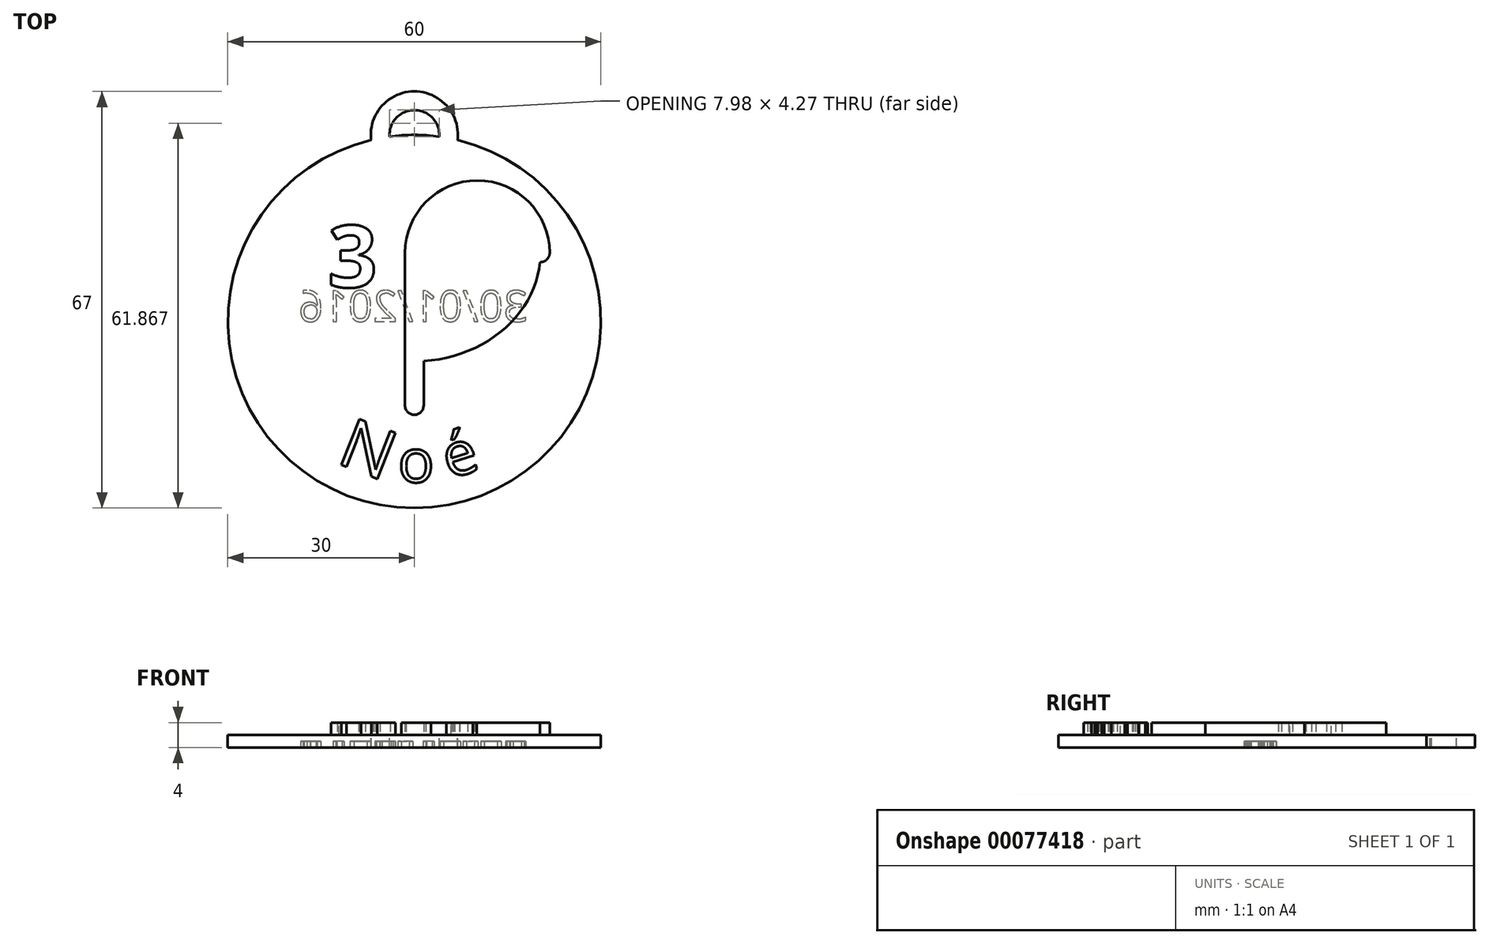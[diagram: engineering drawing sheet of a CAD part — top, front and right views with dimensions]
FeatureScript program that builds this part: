
annotation { "Feature Type Name" : "Feature", "Feature Type Description" : "" }
export const myFeature = defineFeature(function(context is Context, id is Id, definition is map)
    precondition{}
    {
        {
            var Q0;
            Q0=qCreatedBy(makeId("Top.planeOp"),FACE);
            var sketch = newSketch(context, id + "F0", { "sketchPlane" : qUnion([Q0])});
            skCircle(sketch, "E0", {"center": v(0, 0) * mm, "radius": 30 * mm});
            skSolve(sketch);
        }
        {
            var Q0;
            Q0=qSketchRegion(id+"F0",true);
            extrude(context, id + "F1", {"entities" : qUnion([Q0]), "oppositeDirection" : true, "depth" : 2 * mm});
        }
        {
            var Q0;
            Q0=qCreatedBy(makeId("Top.planeOp"),FACE);
            var sketch = newSketch(context, id + "F2", { "sketchPlane" : qUnion([Q0])});
            skEllipticalArc(sketch, "E1", {});
            skLineSegment(sketch, "E2", {"start": v(0, 0) * mm, "end": v(0, 30) * mm, "construction": true});
            skLineSegment(sketch, "E3", {"start": v(0, 11.04) * mm, "end": v(0, -13.5) * mm});
            skArc(sketch, "E4", {"start": v(20.27, 11.04) * mm, "mid": v(10.13, 21.17) * mm, "end": v(0, 11.04) * mm});
            skLineSegment(sketch, "E5", {"start": v(0, 11.04) * mm, "end": v(-16.84, 20.76) * mm, "construction": true});
            skLineSegment(sketch, "E6", {"start": v(0, 11.04) * mm, "end": v(-20.27, 11.04) * mm, "construction": true});
            skArc(sketch, "E7.0.startCap", {"start": v(-1.5, 11.04) * mm, "mid": v(0, 12.54) * mm, "end": v(1.5, 11.04) * mm});
            skArc(sketch, "E7.0.endCap", {"start": v(1.5, -13.5) * mm, "mid": v(0, -15) * mm, "end": v(-1.5, -13.5) * mm});
            skLineSegment(sketch, "E7.0.left", {"start": v(1.5, 11.04) * mm, "end": v(1.5, -13.5) * mm});
            skLineSegment(sketch, "E7.0.right", {"start": v(-1.5, 11.04) * mm, "end": v(-1.5, -13.5) * mm});
            skArc(sketch, "E8.0.startCap", {"start": v(21.77, 11.04) * mm, "mid": v(20.27, 9.54) * mm, "end": v(18.77, 11.04) * mm});
            skArc(sketch, "E8.0.endCap", {"start": v(1.5, 11.04) * mm, "mid": v(0, 9.54) * mm, "end": v(-1.5, 11.04) * mm});
            skArc(sketch, "E8.0.left", {"start": v(18.77, 11.04) * mm, "mid": v(10.13, 19.67) * mm, "end": v(1.5, 11.04) * mm});
            skArc(sketch, "E8.0.right", {"start": v(21.77, 11.04) * mm, "mid": v(10.13, 22.67) * mm, "end": v(-1.5, 11.04) * mm});
            skArc(sketch, "E8.1.startCap", {"start": v(-18.02, 21.68) * mm, "mid": v(-15.91, 21.95) * mm, "end": v(-15.65, 19.84) * mm});
            skArc(sketch, "E8.1.endCap", {"start": v(18.77, 11.04) * mm, "mid": v(20.27, 12.54) * mm, "end": v(21.77, 11.04) * mm});
            skFitSpline(sketch, "E8.1.left", {"points": [v(18.7, 9.5) * mm, v(18.8, 11.04) * mm, v(18.7, 12.6) * mm, v(18.36, 14.63) * mm, v(17.66, 16.6) * mm, v(16.63, 18.49) * mm, v(15.37, 20.3) * mm, v(13.44, 22.32) * mm, v(11.07, 24) * mm, v(8.94, 25.1) * mm, v(6.7, 26.01) * mm, v(4.32, 26.63) * mm, v(1.87, 26.95) * mm, v(0, 27.03) * mm, v(-1.87, 26.95) * mm, v(-4.32, 26.63) * mm, v(-6.7, 26.01) * mm, v(-8.94, 25.1) * mm, v(-11.07, 24) * mm, v(-13.44, 22.32) * mm, v(-15.37, 20.3) * mm, v(-16.63, 18.49) * mm, v(-17.66, 16.6) * mm, v(-18.36, 14.63) * mm, v(-18.7, 12.6) * mm, v(-18.8, 11.04) * mm, v(-18.7, 9.5) * mm, v(-18.36, 7.46) * mm, v(-17.66, 5.48) * mm, v(-16.63, 3.6) * mm, v(-15.37, 1.8) * mm, v(-13.44, -0.24) * mm, v(-11.07, -1.92) * mm, v(-8.94, -3.02) * mm, v(-6.7, -3.93) * mm, v(-4.32, -4.55) * mm, v(-1.87, -4.86) * mm, v(0, -4.94) * mm, v(1.87, -4.86) * mm, v(4.32, -4.55) * mm, v(6.7, -3.93) * mm, v(8.94, -3.02) * mm, v(11.07, -1.92) * mm, v(13.44, -0.24) * mm, v(15.37, 1.8) * mm, v(16.63, 3.6) * mm, v(17.66, 5.48) * mm, v(18.36, 7.46) * mm, v(18.7, 9.5) * mm, v(18.8, 11.04) * mm, v(18.7, 12.6) * mm]});
            skFitSpline(sketch, "E8.1.right", {"points": [v(21.7, 9.15) * mm, v(21.8, 11.04) * mm, v(21.7, 12.93) * mm, v(21.27, 15.42) * mm, v(20.42, 17.81) * mm, v(19.18, 20.07) * mm, v(17.69, 22.22) * mm, v(15.4, 24.61) * mm, v(12.65, 26.56) * mm, v(10.2, 27.83) * mm, v(7.62, 28.88) * mm, v(4.92, 29.58) * mm, v(2.12, 29.94) * mm, v(0, 30.03) * mm, v(-2.12, 29.94) * mm, v(-4.92, 29.58) * mm, v(-7.62, 28.88) * mm, v(-10.2, 27.83) * mm, v(-12.65, 26.56) * mm, v(-15.4, 24.61) * mm, v(-17.69, 22.22) * mm, v(-19.18, 20.07) * mm, v(-20.42, 17.81) * mm, v(-21.27, 15.42) * mm, v(-21.7, 12.93) * mm, v(-21.8, 11.04) * mm, v(-21.7, 9.15) * mm, v(-21.27, 6.67) * mm, v(-20.42, 4.27) * mm, v(-19.18, 2) * mm, v(-17.69, -0.14) * mm, v(-15.4, -2.53) * mm, v(-12.65, -4.48) * mm, v(-10.2, -5.75) * mm, v(-7.62, -6.8) * mm, v(-4.92, -7.5) * mm, v(-2.12, -7.86) * mm, v(0, -7.95) * mm, v(2.12, -7.86) * mm, v(4.92, -7.5) * mm, v(7.62, -6.8) * mm, v(10.2, -5.75) * mm, v(12.65, -4.48) * mm, v(15.4, -2.53) * mm, v(17.69, -0.14) * mm, v(19.18, 2) * mm, v(20.42, 4.27) * mm, v(21.27, 6.67) * mm, v(21.7, 9.15) * mm, v(21.8, 11.04) * mm, v(21.7, 12.93) * mm]});
            const initialGuessF2  = {"E1": [0, 0.011041626236194823, 1, 0, 0.020266667008310185, 0.017458373763805178, 2.5511335140588507, 0]};
            skSetInitialGuess(sketch, initialGuessF2);
            skSolve(sketch);
        }
        {
            var Q0;
            {var subQ0=sQuery(id+"F2.wireOp",EDGE,"E8.1.startCap");Q0=makeQuery(id+"F2.imprint","IMPRINT",FACE,{"disambiguationData":[TD([[makeQuery(id+"F2.imprint","IMPRINT",EDGE,{"derivedFrom":subQ0}),-1.0]])]});}
            var Q1;
            {var subQ0=sQuery(id+"F2.wireOp",EDGE,"E7.0.right");var subQ1=sQuery(id+"F2.wireOp",EDGE,"E1");var subQ2=makeQuery(id+"F2.imprint","INTERSECT",VERTEX,{"derivedFrom":[subQ1,subQ0]});Q1=makeQuery(id+"F2.imprint","IMPRINT",FACE,{"disambiguationData":[TD([[makeQuery(id+"F2.imprint","IMPRINT",EDGE,{"disambiguationData":[TD([[subQ2,-1.0]])],"derivedFrom":subQ1}),1.0]])]});}
            var Q2;
            {var subQ0=sQuery(id+"F2.wireOp",EDGE,"E3");var subQ1=sQuery(id+"F2.wireOp",EDGE,"E1");var subQ2=makeQuery(id+"F2.imprint","INTERSECT",VERTEX,{"derivedFrom":[subQ1,subQ0]});Q2=makeQuery(id+"F2.imprint","IMPRINT",FACE,{"disambiguationData":[TD([[makeQuery(id+"F2.imprint","IMPRINT",EDGE,{"disambiguationData":[TD([[subQ2,-1.0]])],"derivedFrom":subQ1}),1.0]])]});}
            var Q3;
            {var subQ0=sQuery(id+"F2.wireOp",EDGE,"E7.0.right");var subQ1=sQuery(id+"F2.wireOp",EDGE,"E1");var subQ2=makeQuery(id+"F2.imprint","INTERSECT",VERTEX,{"derivedFrom":[subQ1,subQ0]});Q3=makeQuery(id+"F2.imprint","IMPRINT",FACE,{"disambiguationData":[TD([[makeQuery(id+"F2.imprint","IMPRINT",EDGE,{"disambiguationData":[TD([[subQ2,-1.0]])],"derivedFrom":subQ1}),-1.0]])]});}
            var Q4;
            {var subQ0=sQuery(id+"F2.wireOp",EDGE,"E3");var subQ1=sQuery(id+"F2.wireOp",EDGE,"E1");var subQ2=makeQuery(id+"F2.imprint","INTERSECT",VERTEX,{"derivedFrom":[subQ1,subQ0]});Q4=makeQuery(id+"F2.imprint","IMPRINT",FACE,{"disambiguationData":[TD([[makeQuery(id+"F2.imprint","IMPRINT",EDGE,{"disambiguationData":[TD([[subQ2,-1.0]])],"derivedFrom":subQ1}),-1.0]])]});}
            var Q5;
            {var subQ0=sQuery(id+"F2.wireOp",EDGE,"E7.0.left");var subQ1=sQuery(id+"F2.wireOp",EDGE,"E1");var subQ2=makeQuery(id+"F2.imprint","INTERSECT",VERTEX,{"derivedFrom":[subQ1,subQ0]});Q5=makeQuery(id+"F2.imprint","IMPRINT",FACE,{"disambiguationData":[TD([[makeQuery(id+"F2.imprint","IMPRINT",EDGE,{"disambiguationData":[TD([[subQ2,-1.0]])],"derivedFrom":subQ1}),-1.0]])]});}
            var Q6;
            {var subQ0=sQuery(id+"F2.wireOp",EDGE,"E7.0.left");var subQ1=sQuery(id+"F2.wireOp",EDGE,"E1");var subQ2=makeQuery(id+"F2.imprint","INTERSECT",VERTEX,{"derivedFrom":[subQ1,subQ0]});Q6=makeQuery(id+"F2.imprint","IMPRINT",FACE,{"disambiguationData":[TD([[makeQuery(id+"F2.imprint","IMPRINT",EDGE,{"disambiguationData":[TD([[subQ2,-1.0]])],"derivedFrom":subQ1}),1.0]])]});}
            var Q7;
            {var subQ0=sQuery(id+"F2.wireOp",EDGE,"E4");var subQ1=sQuery(id+"F2.wireOp",EDGE,"E1");var subQ2=makeQuery(id+"F2.imprint","INTERSECT",VERTEX,{"derivedFrom":[subQ1,subQ0]});Q7=makeQuery(id+"F2.imprint","IMPRINT",FACE,{"disambiguationData":[TD([[makeQuery(id+"F2.imprint","IMPRINT",EDGE,{"disambiguationData":[TD([[subQ2,1.0]])],"derivedFrom":subQ1}),-1.0]])]});}
            var Q8;
            {var subQ0=sQuery(id+"F2.wireOp",EDGE,"E4");var subQ1=sQuery(id+"F2.wireOp",EDGE,"E1");var subQ2=makeQuery(id+"F2.imprint","INTERSECT",VERTEX,{"derivedFrom":[subQ1,subQ0]});Q8=makeQuery(id+"F2.imprint","IMPRINT",FACE,{"disambiguationData":[TD([[makeQuery(id+"F2.imprint","IMPRINT",EDGE,{"disambiguationData":[TD([[subQ2,1.0]])],"derivedFrom":subQ1}),1.0]])]});}
            var Q9;
            {var subQ5=sQuery(id+"F2.wireOp",EDGE,"E8.0.left");Q9=makeQuery(id+"F2.imprint","IMPRINT",FACE,{"disambiguationData":[TD([[makeQuery(id+"F2.imprint","IMPRINT",EDGE,{"derivedFrom":subQ5}),-1.0]])]});}
            var Q10;
            {var subQ5=sQuery(id+"F2.wireOp",EDGE,"E8.0.right");Q10=makeQuery(id+"F2.imprint","IMPRINT",FACE,{"disambiguationData":[TD([[makeQuery(id+"F2.imprint","IMPRINT",EDGE,{"derivedFrom":subQ5}),1.0]])]});}
            var Q11;
            {var subQ0=sQuery(id+"F2.wireOp",EDGE,"E4");var subQ1=sQuery(id+"F2.wireOp",EDGE,"E3");var subQ2=makeQuery(id+"F2.imprint","INTERSECT",VERTEX,{"derivedFrom":[subQ1,subQ0]});Q11=makeQuery(id+"F2.imprint","IMPRINT",FACE,{"disambiguationData":[TD([[makeQuery(id+"F2.imprint","IMPRINT",EDGE,{"disambiguationData":[TD([[subQ2,-1.0]])],"derivedFrom":subQ1}),-1.0]])]});}
            var Q12;
            {var subQ0=sQuery(id+"F2.wireOp",EDGE,"E4");var subQ1=sQuery(id+"F2.wireOp",EDGE,"E3");var subQ2=makeQuery(id+"F2.imprint","INTERSECT",VERTEX,{"derivedFrom":[subQ1,subQ0]});Q12=makeQuery(id+"F2.imprint","IMPRINT",FACE,{"disambiguationData":[TD([[makeQuery(id+"F2.imprint","IMPRINT",EDGE,{"disambiguationData":[TD([[subQ2,-1.0]])],"derivedFrom":subQ1}),1.0]])]});}
            var Q13;
            {var subQ0=sQuery(id+"F2.wireOp",EDGE,"E8.0.endCap");var subQ1=sQuery(id+"F2.wireOp",EDGE,"E3");var subQ2=makeQuery(id+"F2.imprint","INTERSECT",VERTEX,{"derivedFrom":[subQ1,subQ0]});Q13=makeQuery(id+"F2.imprint","IMPRINT",FACE,{"disambiguationData":[TD([[makeQuery(id+"F2.imprint","IMPRINT",EDGE,{"disambiguationData":[TD([[subQ2,-1.0]])],"derivedFrom":subQ1}),-1.0]])]});}
            var Q14;
            {var subQ0=sQuery(id+"F2.wireOp",EDGE,"E8.0.endCap");var subQ1=sQuery(id+"F2.wireOp",EDGE,"E3");var subQ2=makeQuery(id+"F2.imprint","INTERSECT",VERTEX,{"derivedFrom":[subQ1,subQ0]});Q14=makeQuery(id+"F2.imprint","IMPRINT",FACE,{"disambiguationData":[TD([[makeQuery(id+"F2.imprint","IMPRINT",EDGE,{"disambiguationData":[TD([[subQ2,-1.0]])],"derivedFrom":subQ1}),1.0]])]});}
            var Q15;
            {var subQ1=sQuery(id+"F2.wireOp",EDGE,"E7.0.endCap");Q15=makeQuery(id+"F2.imprint","IMPRINT",FACE,{"disambiguationData":[TD([[makeQuery(id+"F2.imprint","IMPRINT",EDGE,{"derivedFrom":subQ1}),-1.0]])]});}
            extrude(context, id + "F3", {"entities" : qUnion([Q0, Q1, Q2, Q3, Q4, Q5, Q6, Q7, Q8, Q9, Q10, Q11, Q12, Q13, Q14, Q15]), "operationType" : NewBodyOperationType.ADD, "depth" : 2 * mm});
        }
        {
            var Q0;
            Q0=qCreatedBy(makeId("Top.planeOp"),FACE);
            var sketch = newSketch(context, id + "F4", { "sketchPlane" : qUnion([Q0])});
            skText(sketch, "E9", { "text": "3", "fontName": "OpenSans-Bold.ttf"});
            skText(sketch, "E10", { "text": "D", "fontName": "OpenSans-Bold.ttf"});
            const initialGuessF4  = {"E9": [-0.0139, 0.0055, 1, 0, 0.01], "E10": [0.0055, 0.0055, 1, 0, 0.01]};
            skSetInitialGuess(sketch, initialGuessF4);
            skSolve(sketch);
        }
        {
            var Q0;
            Q0=qSketchRegion(id+"F4",true);
            extrude(context, id + "F5", {"entities" : qUnion([Q0]), "operationType" : NewBodyOperationType.ADD, "depth" : 2 * mm});
        }
        {
            var Q0;
            {var subQ8=sQuery(id+"F0.wireOp",EDGE,"E0");Q0=makeQuery(id+"F3.boolean.opBoolean","SPLIT",FACE,{"disambiguationData":[TD([makeQuery(id+"F1.opExtrude","SWEPT_FACE",FACE,{"disambiguationData":[OSD([subQ8])]})])],"derivedFrom":makeQuery(id+"F1.opExtrude","CAP_FACE",FACE,{"disambiguationData":[OSD([subQ8])],"isStart":true})});}
            var sketch = newSketch(context, id + "F6", { "sketchPlane" : qUnion([Q0])});
            skCircle(sketch, "E11.0", {"center": v(0, 0) * mm, "radius": 26 * mm, "construction": true});
            skText(sketch, "E12", { "text": "N", "fontName": "OpenSans-Regular.ttf"});
            skText(sketch, "E13", { "text": "o", "fontName": "OpenSans-Regular.ttf"});
            skText(sketch, "E14", { "text": "é", "fontName": "OpenSans-Regular.ttf"});
            const initialGuessF6  = {"E12": [-0.01273, -0.02267, 0.93191, -0.36269, 0.008], "E13": [-0.00266, -0.02586, 1, 0, 0.007], "E14": [0.00565, -0.02538, 0.95098, 0.30925, 0.007]};
            skSetInitialGuess(sketch, initialGuessF6);
            skSolve(sketch);
        }
        {
            var Q0;
            Q0=qSketchRegion(id+"F6",true);
            extrude(context, id + "F7", {"entities" : qUnion([Q0]), "operationType" : NewBodyOperationType.ADD, "depth" : 2 * mm});
        }
        {
            var Q0;
            Q0=qCreatedBy(makeId("Top.planeOp"),FACE);
            var sketch = newSketch(context, id + "F8", { "sketchPlane" : qUnion([Q0])});
            skArc(sketch, "E15", {"start": v(5.48, 29.5) * mm, "mid": v(0, 35.5) * mm, "end": v(-5.48, 29.5) * mm});
            skArc(sketch, "E16.0.startCap", {"start": v(6.97, 29.36) * mm, "mid": v(5.34, 28) * mm, "end": v(3.98, 29.63) * mm});
            skArc(sketch, "E16.0.endCap", {"start": v(-3.98, 29.63) * mm, "mid": v(-5.34, 28) * mm, "end": v(-6.97, 29.36) * mm});
            skArc(sketch, "E16.0.left", {"start": v(3.98, 29.63) * mm, "mid": v(0, 34) * mm, "end": v(-3.98, 29.63) * mm});
            skArc(sketch, "E16.0.right", {"start": v(6.97, 29.36) * mm, "mid": v(0, 37) * mm, "end": v(-6.97, 29.36) * mm});
            skSolve(sketch);
        }
        {
            var Q0;
            Q0=qSketchRegion(id+"F8",true);
            extrude(context, id + "F9", {"entities" : qUnion([Q0]), "operationType" : NewBodyOperationType.ADD, "oppositeDirection" : true, "depth" : 2 * mm});
        }
        {
            var Q0;
            Q0=makeQuery(id+"F9.boolean.opBoolean","MERGE",FACE,{"derivedFrom":[makeQuery(id+"F1.opExtrude","CAP_FACE",FACE,{"disambiguationData":[OSD([sQuery(id+"F0.wireOp",EDGE,"E0")])],"isStart":false}),makeQuery(id+"F9.opExtrude","CAP_FACE",FACE,{"disambiguationData":[OSD([sQuery(id+"F8.wireOp",EDGE,"E16.0.startCap"),sQuery(id+"F8.wireOp",EDGE,"E16.0.endCap"),sQuery(id+"F8.wireOp",EDGE,"E16.0.left"),sQuery(id+"F8.wireOp",EDGE,"E16.0.right")])],"isStart":false})]});
            var sketch = newSketch(context, id + "F10", { "sketchPlane" : qUnion([Q0])});
            skText(sketch, "E17", { "text": "30/01/2016", "fontName": "OpenSans-Regular.ttf"});
            const initialGuessF10  = {"E17": [0.01826, 0, -1, 0, 0.005]};
            skSetInitialGuess(sketch, initialGuessF10);
            skSolve(sketch);
        }
        {
            var Q0;
            Q0=qSketchRegion(id+"F10",true);
            extrude(context, id + "F11", {"entities" : qUnion([Q0]), "operationType" : NewBodyOperationType.REMOVE, "oppositeDirection" : true, "depth" : 1 * mm});
        }
    });
